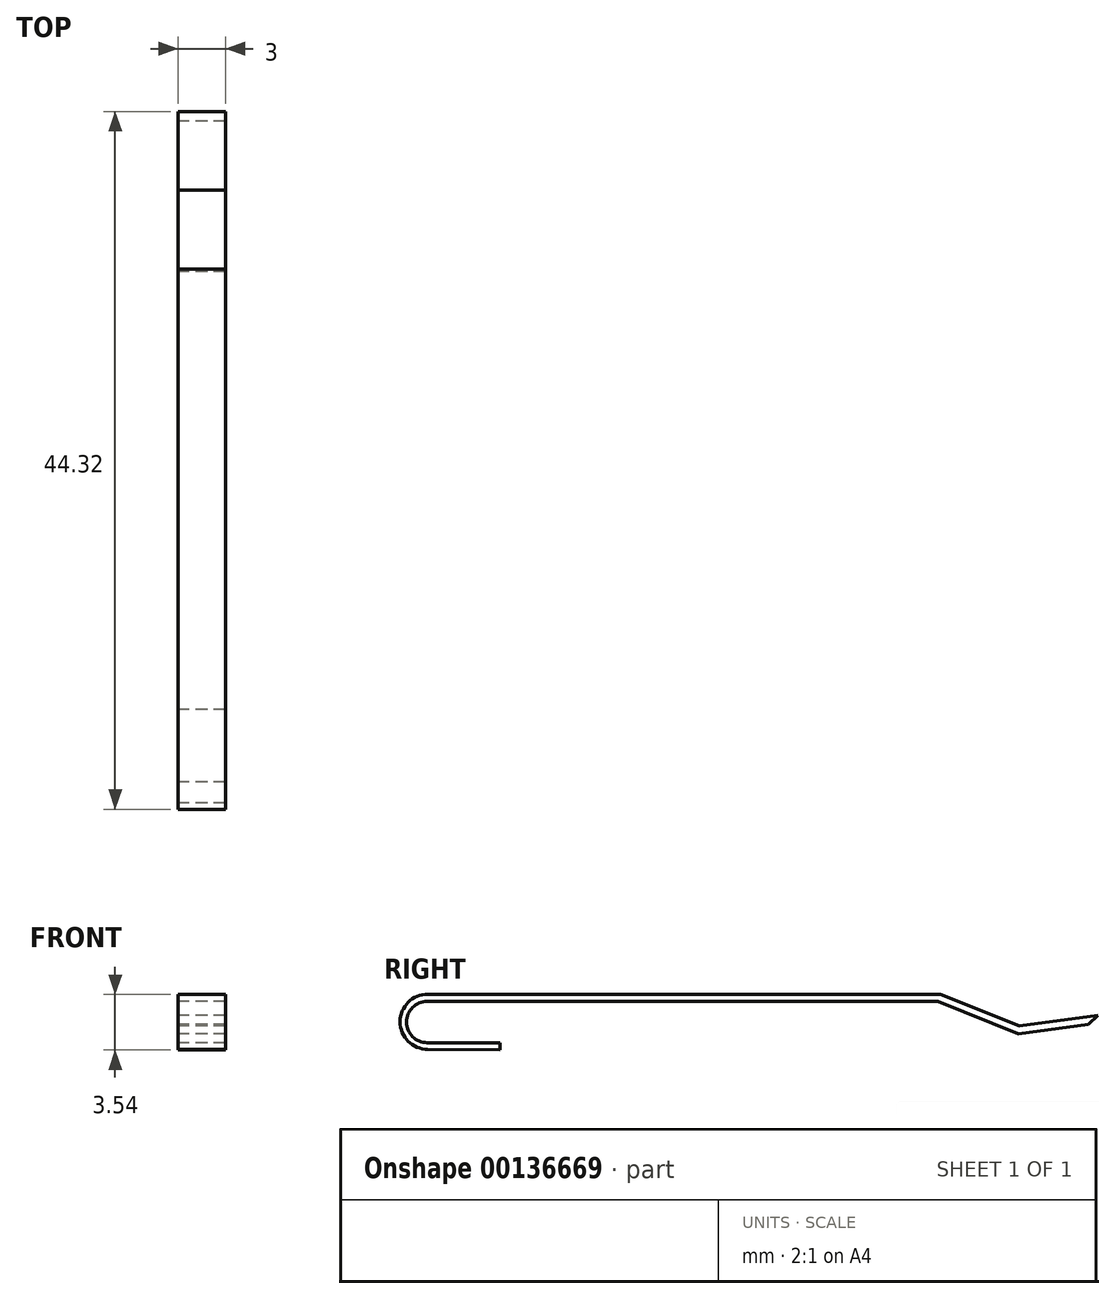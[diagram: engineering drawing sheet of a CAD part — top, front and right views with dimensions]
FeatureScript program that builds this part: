
annotation { "Feature Type Name" : "Feature", "Feature Type Description" : "" }
export const myFeature = defineFeature(function(context is Context, id is Id, definition is map)
    precondition{}
    {
        {
            var Q0;
            Q0=qCreatedBy(makeId("Right.planeOp"),FACE);
            var sketch = newSketch(context, id + "F0", { "sketchPlane" : qUnion([Q0])});
            skLineSegment(sketch, "E0", {"start": v(-20.85, 1.15) * mm, "end": v(-25.85, 0.5) * mm});
            skLineSegment(sketch, "E1", {"start": v(-30.85, 2.5) * mm, "end": v(-25.85, 0.5) * mm});
            skLineSegment(sketch, "E2", {"start": v(-31.01, 2.05) * mm, "end": v(-58.54, 2.05) * mm});
            skLineSegment(sketch, "E3", {"start": v(-30.85, 2.5) * mm, "end": v(-63.42, 2.5) * mm});
            skLineSegment(sketch, "E4", {"start": v(-31.01, 2.05) * mm, "end": v(-25.9, 0) * mm});
            skLineSegment(sketch, "E5", {"start": v(-25.9, 0) * mm, "end": v(-21.45, 0.59) * mm});
            skLineSegment(sketch, "E6", {"start": v(-21.45, 0.59) * mm, "end": v(-20.85, 1.15) * mm});
            skPoint(sketch, "E7.end.orphan", {"position": v(-58.54, 0.54) * mm});
            skLineSegment(sketch, "E8", {"start": v(-58.54, 2.05) * mm, "end": v(-63.45, 2.05) * mm});
            skPoint(sketch, "E9.center.orphan", {"position": v(-63.46, 1.25) * mm});
            skPoint(sketch, "E10.start.orphan", {"position": v(-63.46, 0.53) * mm});
            skPoint(sketch, "E11.end.orphan", {"position": v(-63.42, 0) * mm});
            skArc(sketch, "E12", {"start": v(-63.45, 2.05) * mm, "mid": v(-64.76, 0.74) * mm, "end": v(-63.45, -0.57) * mm});
            skArc(sketch, "E13", {"start": v(-63.42, 2.5) * mm, "mid": v(-65.17, 0.75) * mm, "end": v(-63.42, -1) * mm});
            skLineSegment(sketch, "E14", {"start": v(-63.45, -0.57) * mm, "end": v(-58.82, -0.57) * mm});
            skLineSegment(sketch, "E15", {"start": v(-58.82, -0.57) * mm, "end": v(-58.82, -1.04) * mm});
            skLineSegment(sketch, "E16", {"start": v(-58.82, -1.04) * mm, "end": v(-63.42, -1) * mm});
            skSolve(sketch);
        }
        {
            var Q0;
            Q0 = qSketchRegion(id + "F0", true);
            extrude(context, id + "F1", {"entities" : qUnion([Q0]), "depth" : 1.5 * mm, "hasSecondDirection" : true, "secondDirectionOppositeDirection" : true, "secondDirectionDepth" : 1.5 * mm});
        }
    });
